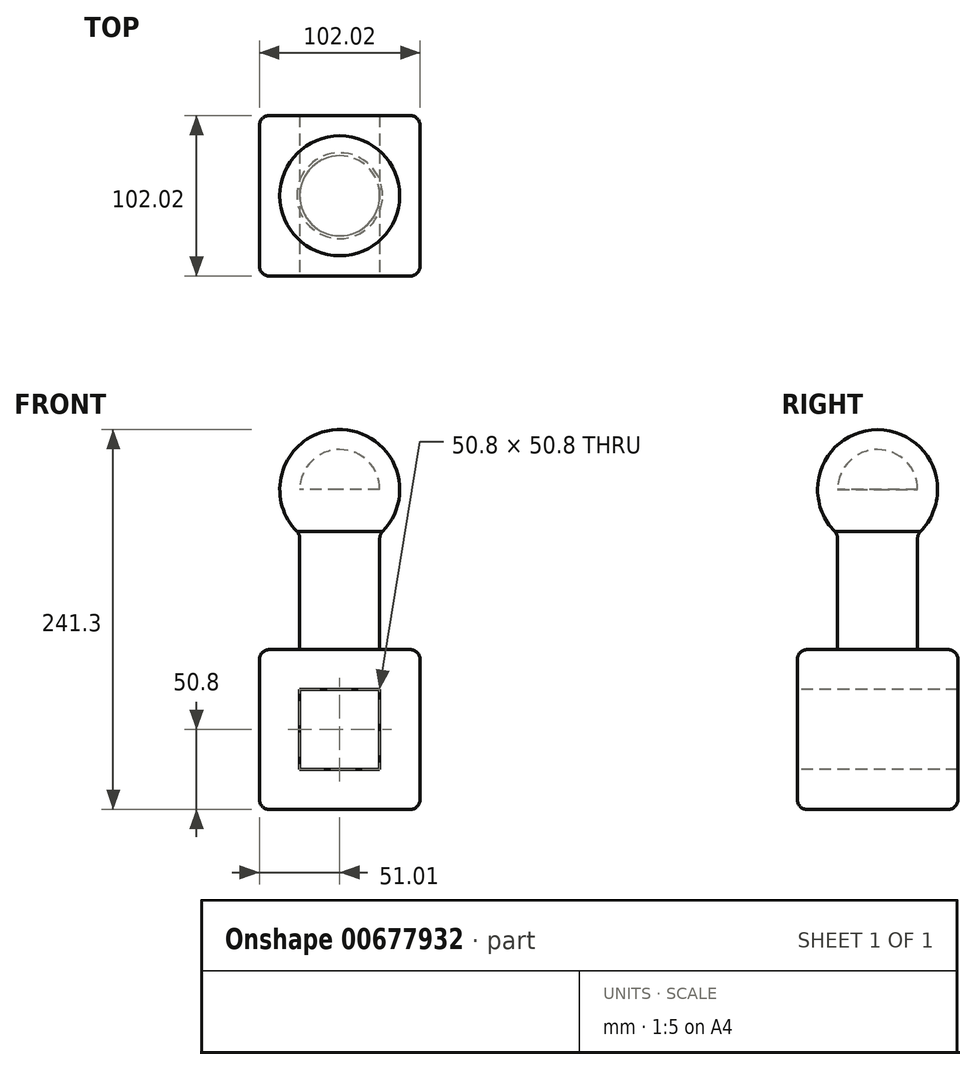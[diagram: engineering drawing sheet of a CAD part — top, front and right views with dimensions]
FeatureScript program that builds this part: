
annotation { "Feature Type Name" : "Feature", "Feature Type Description" : "" }
export const myFeature = defineFeature(function(context is Context, id is Id, definition is map)
    precondition{}
    {
        {
            var Q0;
            Q0=qCreatedBy(makeId("Top.planeOp"),FACE);
            var sketch = newSketch(context, id + "F0", { "sketchPlane" : qUnion([Q0])});
            skLineSegment(sketch, "E0.bottom", {"start": v(51.01, -51.01) * mm, "end": v(-51.01, -51.01) * mm});
            skLineSegment(sketch, "E0.top", {"start": v(51.01, 51.01) * mm, "end": v(-51.01, 51.01) * mm});
            skLineSegment(sketch, "E0.left", {"start": v(51.01, -51.01) * mm, "end": v(51.01, 51.01) * mm});
            skLineSegment(sketch, "E0.right", {"start": v(-51.01, -51.01) * mm, "end": v(-51.01, 51.01) * mm});
            skPoint(sketch, "E0.middle", {"position": v(0, 0) * mm});
            skSolve(sketch);
        }
        {
            var Q0;
            Q0 = qSketchRegion(id + "F0", true);
            extrude(context, id + "F1", {"entities" : qUnion([Q0]), "depth" : 101.6 * mm, "offsetDistance" : 25.4 * mm});
        }
        {
            var Q0;
            Q0=makeQuery(id+"F1.opExtrude","CAP_FACE",FACE,{"disambiguationData":[OSD([sQuery(id+"F0.wireOp",EDGE,"E0.bottom"),sQuery(id+"F0.wireOp",EDGE,"E0.top"),sQuery(id+"F0.wireOp",EDGE,"E0.left"),sQuery(id+"F0.wireOp",EDGE,"E0.right")])],"isStart":false});
            var sketch = newSketch(context, id + "F2", { "sketchPlane" : qUnion([Q0])});
            skCircle(sketch, "E1", {"center": v(0, 0) * mm, "radius": 25.4 * mm});
            skSolve(sketch);
        }
        {
            var Q0;
            Q0=makeQuery(id+"F2.imprint","IMPRINT",FACE,{"disambiguationData":[TD([[makeQuery(id+"F2.imprint","IMPRINT",EDGE,{"derivedFrom":sQuery(id+"F2.wireOp",EDGE,"E1")}),1.0]])]});
            extrude(context, id + "F3", {"entities" : qUnion([Q0]), "operationType" : NewBodyOperationType.ADD, "depth" : 101.6 * mm, "offsetDistance" : 25.4 * mm});
        }
        {
            var Q0;
            Q0=makeQuery(id+"F3.opExtrude","CAP_FACE",FACE,{"disambiguationData":[OSD([sQuery(id+"F2.wireOp",EDGE,"E1")])],"isStart":false});
            var sketch = newSketch(context, id + "F4", { "sketchPlane" : qUnion([Q0])});
            skArc(sketch, "E2", {"start": v(0, -38.1) * mm, "mid": v(38.1, 0) * mm, "end": v(0, 38.1) * mm});
            skLineSegment(sketch, "E3", {"start": v(0, 0) * mm, "end": v(0, 38.1) * mm});
            skLineSegment(sketch, "E4", {"start": v(0, 38.1) * mm, "end": v(0, -38.1) * mm});
            skSolve(sketch);
        }
        {
            var Q0;
            {var subQ0=sQuery(id+"F4.wireOp",EDGE,"E4");var subQ1=makeQuery(id+"F4.imprint","IMPRINT",VERTEX,{"derivedFrom":subQ0});Q0=makeQuery(id+"F4.imprint","IMPRINT",FACE,{"disambiguationData":[TD([[makeQuery(id+"F4.imprint","IMPRINT",EDGE,{"disambiguationData":[TD([[subQ1,1.0]])],"derivedFrom":subQ0}),1.0]])]});}
            var Q1;
            {var subQ0=sQuery(id+"F4.wireOp",EDGE,"E2");Q1=makeQuery(id+"F4.imprint","IMPRINT",FACE,{"disambiguationData":[TD([[makeQuery(id+"F4.imprint","IMPRINT",EDGE,{"derivedFrom":subQ0}),1.0]])]});}
            var Q2;
            Q2=sQuery(id+"F4.wireOp",EDGE,"E4");
            revolve(context, id + "F5", {"operationType" : NewBodyOperationType.ADD, "entities" : qUnion([Q0, Q1]), "axis" : qUnion([Q2]), "revolveType" : RevolveType.FULL});
        }
        {
            var Q0;
            Q0=makeQuery(id+"F1.opExtrude","SWEPT_FACE",FACE,{"disambiguationData":[OSD([sQuery(id+"F0.wireOp",EDGE,"E0.bottom")])]});
            var sketch = newSketch(context, id + "F6", { "sketchPlane" : qUnion([Q0])});
            skLineSegment(sketch, "E5.bottom", {"start": v(25.4, 25.4) * mm, "end": v(-25.4, 25.4) * mm});
            skLineSegment(sketch, "E5.top", {"start": v(25.4, 76.2) * mm, "end": v(-25.4, 76.2) * mm});
            skLineSegment(sketch, "E5.left", {"start": v(25.4, 25.4) * mm, "end": v(25.4, 76.2) * mm});
            skLineSegment(sketch, "E5.right", {"start": v(-25.4, 25.4) * mm, "end": v(-25.4, 76.2) * mm});
            skPoint(sketch, "E5.middle", {"position": v(0, 50.8) * mm});
            skSolve(sketch);
        }
        {
            var Q0;
            Q0 = qSketchRegion(id + "F6", true);
            extrude(context, id + "F7", {"entities" : qUnion([Q0]), "operationType" : NewBodyOperationType.REMOVE, "oppositeDirection" : true, "depth" : 130.05 * mm, "offsetDistance" : 25.4 * mm});
        }
        {
            var Q0;
            Q0=makeQuery(id+"F1.opExtrude","CAP_EDGE",EDGE,{"disambiguationData":[OSD([sQuery(id+"F0.wireOp",EDGE,"E0.left")])],"isStart":false});
            var Q1;
            Q1=makeQuery(id+"F1.opExtrude","SWEPT_EDGE",EDGE,{"disambiguationData":[OSD([sQuery(id+"F0.wireOp",EDGE,"E0.bottom"),sQuery(id+"F0.wireOp",EDGE,"E0.left")])]});
            var Q2;
            Q2=makeQuery(id+"F1.opExtrude","CAP_EDGE",EDGE,{"disambiguationData":[OSD([sQuery(id+"F0.wireOp",EDGE,"E0.left")])],"isStart":true});
            var Q3;
            Q3=makeQuery(id+"F1.opExtrude","SWEPT_EDGE",EDGE,{"disambiguationData":[OSD([sQuery(id+"F0.wireOp",EDGE,"E0.top"),sQuery(id+"F0.wireOp",EDGE,"E0.left")])]});
            var Q4;
            Q4=makeQuery(id+"F1.opExtrude","CAP_EDGE",EDGE,{"disambiguationData":[OSD([sQuery(id+"F0.wireOp",EDGE,"E0.bottom")])],"isStart":false});
            var Q5;
            Q5=makeQuery(id+"F1.opExtrude","CAP_EDGE",EDGE,{"disambiguationData":[OSD([sQuery(id+"F0.wireOp",EDGE,"E0.bottom")])],"isStart":true});
            var Q6;
            Q6=makeQuery(id+"F1.opExtrude","SWEPT_EDGE",EDGE,{"disambiguationData":[OSD([sQuery(id+"F0.wireOp",EDGE,"E0.bottom"),sQuery(id+"F0.wireOp",EDGE,"E0.right")])]});
            var Q7;
            Q7=makeQuery(id+"F1.opExtrude","CAP_EDGE",EDGE,{"disambiguationData":[OSD([sQuery(id+"F0.wireOp",EDGE,"E0.right")])],"isStart":false});
            var Q8;
            Q8=makeQuery(id+"F1.opExtrude","CAP_EDGE",EDGE,{"disambiguationData":[OSD([sQuery(id+"F0.wireOp",EDGE,"E0.top")])],"isStart":false});
            var Q9;
            Q9=makeQuery(id+"F1.opExtrude","SWEPT_EDGE",EDGE,{"disambiguationData":[OSD([sQuery(id+"F0.wireOp",EDGE,"E0.top"),sQuery(id+"F0.wireOp",EDGE,"E0.right")])]});
            var Q10;
            Q10=makeQuery(id+"F1.opExtrude","CAP_EDGE",EDGE,{"disambiguationData":[OSD([sQuery(id+"F0.wireOp",EDGE,"E0.top")])],"isStart":true});
            var Q11;
            Q11=makeQuery(id+"F1.opExtrude","CAP_EDGE",EDGE,{"disambiguationData":[OSD([sQuery(id+"F0.wireOp",EDGE,"E0.right")])],"isStart":true});
            var Q12;
            Q12=makeQuery(id+"F3.opExtrude","CAP_EDGE",EDGE,{"disambiguationData":[OSD([sQuery(id+"F2.wireOp",EDGE,"E1")])],"isStart":true});
            var Q13;
            Q13=makeQuery(id+"F5.boolean.opBoolean","INTERSECT",EDGE,{"derivedFrom":[makeQuery(id+"F3.opExtrude","SWEPT_FACE",FACE,{"disambiguationData":[OSD([sQuery(id+"F2.wireOp",EDGE,"E1")])]}),makeQuery(id+"F5.opRevolve","SWEPT_FACE",FACE,{"disambiguationData":[OSD([sQuery(id+"F4.wireOp",EDGE,"E2")])]})]});
            fillet(context, id + "F8", {"entities" : qUnion([Q0, Q1, Q2, Q3, Q4, Q5, Q6, Q7, Q8, Q9, Q10, Q11, Q12, Q13]), "radius" : 6.35 * mm, "tangentPropagation" : true, "allowEdgeOverflow" : false});
        }
    });
